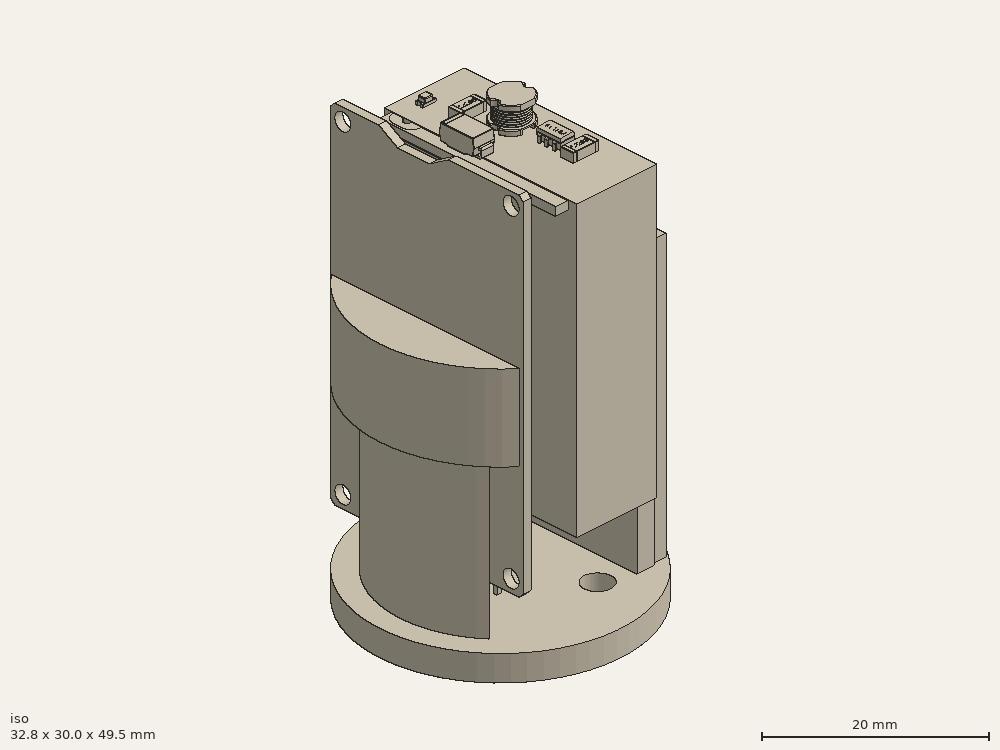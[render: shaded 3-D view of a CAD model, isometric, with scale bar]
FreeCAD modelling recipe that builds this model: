
FCSTD DOCUMENT  (FreeCAD 1.0R39319 (Git))
Label: case
License: All rights reserved
LicenseURL: https://en.wikipedia.org/wiki/All_rights_reserved
objects: Part::Feature×26, Sketcher::SketchObject×12, PartDesign::Pad×8, PartDesign::Pocket×6, PartDesign::Body×2, Assembly::JointGroup×1, Part::Compound2×1, Assembly::AssemblyObject×1
note: 94 computed .brp shape members not serialized (recipe doc carries the construction recipe); baked Part::Feature solids carry a one-line shape summary decoded from their .brp

FEATURE [Assembly::JointGroup] Joints
FEATURE [Part::Feature] Solid  label="SD"
  Placement = pos=(-9.17,6e-15,27) rot=(0.57735,0.57735,0.57735;4.18879rad)
  shape: bbox 4 x 24 x 44.75 mm, 1523 faces (baked)
FEATURE [Part::Feature] Solid024  label="ProMini"
  Placement = pos=(11.482,-0.307405,17.75) rot=(0,1,0;4.71239rad)
  shape: bbox 4.104 x 17.78 x 33.02 mm, 2932 faces (baked)
FEATURE [Part::Feature] Feature  label="mini_dc_dc001"
  Placement = pos=(16,-7.5,27.5) rot=(0,0,1;1.5708rad)
  shape: bbox 11 x 22 x 4.21 mm, 1273 faces, 17 solids (baked)
FEATURE [Sketcher::SketchObject] Sketch001
  ArcFitTolerance = 1e-06
  AttachmentSupport = -> [XY_Plane001]
  FullyConstrained = true
  MakeInternals = false
  MapMode = 5
  sketch-geometry (1):
    g0: Circle CenterX=0 CenterY=0 CenterZ=0 NormalX=0 NormalY=0 NormalZ=1 AngleXU=0 Radius=16.5
  constraints (2):
    c: Diameter(g0) = 33
    c: Coincident(g0,g-1)
FEATURE [PartDesign::Pad] Pad
  Direction = (0,0,1)
  Length = 1
  Length2 = 10
  Profile = -> Sketch001
  ReferenceAxis = -> Sketch001 [N_Axis]
  Refine = true
  Suppressed = false
  Type = 0
FEATURE [Part::Feature] Solid026 .. Solid033  x8 (patterned run collapsed; names and placements below)
  shape: bbox 2.54 x 11.18 x 2.54 mm, 32 faces (baked)
FEATURE [Part::Feature] Solid034
  shape: bbox 5.403 x 0.9032 x 5.403 mm, 256 faces (baked)
FEATURE [Part::Feature] Solid035
  shape: bbox 3.012 x 1.362 x 3.662 mm, 115 faces (baked)
FEATURE [Part::Feature] Solid036
  shape: bbox 2.765 x 1.061 x 0.8748 mm, 38 faces (baked)
FEATURE [Part::Feature] Solid037
  shape: bbox 0.8748 x 1.061 x 2.765 mm, 38 faces (baked)
FEATURE [Part::Feature] Solid038
  shape: bbox 0.8775 x 0.4775 x 2.468 mm, 43 faces (baked)
FEATURE [Part::Feature] Solid039
  shape: bbox 0.8775 x 0.4775 x 2.468 mm, 43 faces (baked)
FEATURE [Part::Feature] Solid040
  shape: bbox 0.8748 x 1.061 x 2.765 mm, 38 faces (baked)
FEATURE [Part::Feature] Solid041
  shape: bbox 0.8748 x 1.061 x 2.765 mm, 38 faces (baked)
FEATURE [Part::Feature] Solid042
  shape: bbox 0.8748 x 1.061 x 2.765 mm, 38 faces (baked)
FEATURE [Part::Feature] Solid043
  shape: bbox 0.8775 x 0.4775 x 2.468 mm, 43 faces (baked)
FEATURE [Part::Feature] Solid044
  shape: bbox 0.8748 x 1.061 x 2.765 mm, 38 faces (baked)
FEATURE [Part::Feature] Solid045
  shape: bbox 0.85 x 0.84 x 1.9 mm, 36 faces (baked)
FEATURE [Part::Feature] Solid046
  shape: bbox 0.8775 x 0.4775 x 2.468 mm, 43 faces (baked)
FEATURE [Part::Feature] Solid047
  shape: bbox 4.2 x 1.693 x 1.6 mm, 44 faces (baked)
FEATURE [Part::Feature] Solid025
  shape: bbox 21.11 x 1.143 x 15.75 mm, 16 faces (baked)
FEATURE [Part::Compound2] Compound  label="mpu"
  Links = -> [Solid025,Solid026,Solid027,Solid028,Solid029,Solid030,Solid031,Solid032,Solid033,Solid034,Solid035,Solid036,Solid037,Solid038,Solid039,Solid040,Solid041,Solid042,Solid043,Solid044,Solid045,Solid046,Solid047]
  Placement = pos=(-17.45,-7.25,-9.5) rot=(0.57735,0.57735,0.57735;2.0944rad)
FEATURE [Sketcher::SketchObject] Sketch002
  ArcFitTolerance = 1e-06
  AttachmentSupport = -> [XY_Plane002]
  FullyConstrained = true
  MakeInternals = false
  MapMode = 5
  sketch-geometry (4):
    g0: LineSegment StartX=0 StartY=0 StartZ=0 EndX=0 EndY=-24 EndZ=0
    g1: LineSegment StartX=0 StartY=-24 StartZ=0 EndX=34 EndY=-24 EndZ=0
    g2: LineSegment StartX=34 StartY=-24 StartZ=0 EndX=34 EndY=0 EndZ=0
    g3: LineSegment StartX=34 StartY=0 StartZ=0 EndX=0 EndY=0 EndZ=0
  constraints (11):
    c: Coincident(g0,g1)
    c: Coincident(g1,g2)
    c: Coincident(g2,g3)
    c: Coincident(g3,g0)
    c: Vertical(g0)
    c: Vertical(g2)
    c: Horizontal(g1)
    c: Horizontal(g3)
    c: Distance(g0,g2) = 34
    c: Distance(g1,g3) = 24
    c: Coincident(g0,g-1)
FEATURE [PartDesign::Pad] Pad001
  Direction = (0,0,1)
  Length = 10
  Length2 = 10
  Profile = -> Sketch002
  ReferenceAxis = -> Sketch002 [N_Axis]
  Refine = true
  Suppressed = false
  Type = 0
FEATURE [PartDesign::Body] Body001  label="lipo"
  AllowCompound = false
  Group = -> [Sketch002,Pad001]
  Origin = -> Origin002
  Placement = pos=(7.5,12,10.07) rot=(0,1,0;4.71239rad)
  Tip = -> Pad001
FEATURE [Sketcher::SketchObject] Sketch003
  ArcFitTolerance = 1e-06
  AttachmentSupport = -> [XY_Plane001]
  FullyConstrained = false
  MakeInternals = false
  MapMode = 5
  sketch-geometry (4):
    g0: LineSegment StartX=-10.1025 StartY=7.19243 StartZ=0 EndX=-10.8313 EndY=7.19243 EndZ=0
    g1: LineSegment StartX=-10.8313 StartY=7.19243 StartZ=0 EndX=-10.8313 EndY=-7.43647 EndZ=0
    g2: LineSegment StartX=-10.8313 StartY=-7.43647 StartZ=0 EndX=-10.1025 EndY=-7.43647 EndZ=0
    g3: LineSegment StartX=-10.1025 StartY=-7.43647 StartZ=0 EndX=-10.1025 EndY=7.19243 EndZ=0
  constraints (8):
    c: Coincident(g0,g1)
    c: Coincident(g1,g2)
    c: Coincident(g2,g3)
    c: Coincident(g3,g0)
    c: Horizontal(g0)
    c: Horizontal(g2)
    c: Vertical(g1)
    c: Vertical(g3)
FEATURE [Sketcher::SketchObject] Sketch004
  ArcFitTolerance = 1e-06
  AttachmentSupport = -> [Pad]
  FullyConstrained = false
  MakeInternals = false
  MapMode = 5
  Placement = pos=(0,0,1) rot=(0,0,1;0rad)
  sketch-geometry (4):
    g0: LineSegment StartX=-10.0742 StartY=4.3685 StartZ=0 EndX=-11.0742 EndY=4.3685 EndZ=0
    g1: LineSegment StartX=-11.0742 StartY=4.3685 StartZ=0 EndX=-11.0742 EndY=-5.47094 EndZ=0
    g2: LineSegment StartX=-11.0742 StartY=-5.47094 StartZ=0 EndX=-10.0742 EndY=-5.47094 EndZ=0
    g3: LineSegment StartX=-10.0742 StartY=-5.47094 StartZ=0 EndX=-10.0742 EndY=4.3685 EndZ=0
  constraints (9):
    c: Coincident(g0,g1)
    c: Coincident(g1,g2)
    c: Coincident(g2,g3)
    c: Coincident(g3,g0)
    c: Horizontal(g0)
    c: Horizontal(g2)
    c: Vertical(g1)
    c: Vertical(g3)
    c: Distance(g1,g3) = 1
FEATURE [PartDesign::Pocket] Pocket
  BaseFeature = -> Pad
  Direction = (0,0,-1)
  Length = 5
  Length2 = 5
  Profile = -> Sketch004
  ReferenceAxis = -> Sketch004 [N_Axis]
  Refine = true
  Suppressed = false
  Type = 0
FEATURE [Sketcher::SketchObject] Sketch005
  ArcFitTolerance = 1e-06
  AttachmentSupport = -> [Pocket]
  FullyConstrained = false
  MakeInternals = false
  MapMode = 5
  Placement = pos=(0,0,1) rot=(0,0,1;0rad)
  sketch-geometry (4):
    g0: LineSegment StartX=9.95573 StartY=8.56673 StartZ=0 EndX=7.83459 EndY=8.56673 EndZ=0
    g1: LineSegment StartX=7.83459 StartY=8.56673 StartZ=0 EndX=7.83459 EndY=-9.23192 EndZ=0
    g2: LineSegment StartX=7.83459 StartY=-9.23192 StartZ=0 EndX=9.95573 EndY=-9.23192 EndZ=0
    g3: LineSegment StartX=9.95573 StartY=-9.23192 StartZ=0 EndX=9.95573 EndY=8.56673 EndZ=0
  constraints (8):
    c: Coincident(g0,g1)
    c: Coincident(g1,g2)
    c: Coincident(g2,g3)
    c: Coincident(g3,g0)
    c: Horizontal(g0)
    c: Horizontal(g2)
    c: Vertical(g1)
    c: Vertical(g3)
FEATURE [PartDesign::Pad] Pad002
  BaseFeature = -> Pocket
  Direction = (0,0,1)
  Length = 30
  Length2 = 10
  Profile = -> Sketch005
  ReferenceAxis = -> Sketch005 [N_Axis]
  Refine = true
  Suppressed = false
  Type = 0
FEATURE [Sketcher::SketchObject] Sketch006
  ArcFitTolerance = 1e-06
  AttachmentSupport = -> [Pad002]
  FullyConstrained = false
  MakeInternals = false
  MapMode = 5
  Placement = pos=(0,0,0) rot=(1,0,0;3.14159rad)
  sketch-geometry (2):
    g0: LineSegment StartX=-9.46997 StartY=8.10814 StartZ=0 EndX=-9.46997 EndY=-8.10814 EndZ=0
    g1: ArcOfCircle CenterX=0 CenterY=0 CenterZ=0 NormalX=0 NormalY=0 NormalZ=1 AngleXU=0 Radius=12.4668 StartAngle=2.43351 EndAngle=3.84967
  constraints (3):
    c: Vertical(g0)
    c: Coincident(g1,g0)
    c: Coincident(g1,g0)
FEATURE [PartDesign::Pad] Pad003
  BaseFeature = -> Pad002
  Direction = (0,0,-1)
  Length = 30
  Length2 = 10
  Profile = -> Sketch006
  ReferenceAxis = -> Sketch006 [N_Axis]
  Refine = true
  Reversed = true
  Suppressed = false
  Type = 0
FEATURE [Sketcher::SketchObject] Sketch007
  ArcFitTolerance = 1e-06
  AttachmentSupport = -> [Pad003]
  FullyConstrained = false
  MakeInternals = false
  MapMode = 5
  Placement = pos=(7.83459,0,0) rot=(0.57735,-0.57735,-0.57735;2.0944rad)
  sketch-geometry (4):
    g0: LineSegment StartX=-10 StartY=6.21939 StartZ=0 EndX=-10 EndY=5.1638 EndZ=0
    g1: LineSegment StartX=-10 StartY=5.1638 StartZ=0 EndX=10 EndY=5.1638 EndZ=0
    g2: LineSegment StartX=10 StartY=5.1638 StartZ=0 EndX=10 EndY=6.21939 EndZ=0
    g3: LineSegment StartX=10 StartY=6.21939 StartZ=0 EndX=-10 EndY=6.21939 EndZ=0
  constraints (8):
    c: Coincident(g0,g1)
    c: Coincident(g1,g2)
    c: Coincident(g2,g3)
    c: Coincident(g3,g0)
    c: Vertical(g0)
    c: Vertical(g2)
    c: Horizontal(g1)
    c: Horizontal(g3)
FEATURE [PartDesign::Pad] Pad004
  BaseFeature = -> Pad003
  Direction = (-1,0,0)
  Length = 3
  Length2 = 10
  Profile = -> Sketch007
  ReferenceAxis = -> Sketch007 [N_Axis]
  Refine = true
  Suppressed = false
  Type = 0
FEATURE [Sketcher::SketchObject] Sketch
  ArcFitTolerance = 1e-06
  AttachmentSupport = -> [Pad004]
  FullyConstrained = false
  MakeInternals = false
  MapMode = 5
  Placement = pos=(0,0,30) rot=(0,0,1;0rad)
  sketch-geometry (2):
    g0: ArcOfCircle CenterX=0 CenterY=-0.00563305 CenterZ=0 NormalX=0 NormalY=0 NormalZ=1 AngleXU=0 Radius=16.4954 StartAngle=2.17527 EndAngle=4.10791
    g1: LineSegment StartX=-9.37485 StartY=13.5667 StartZ=0 EndX=-9.37485 EndY=-13.578 EndZ=0
  constraints (3):
    c: Coincident(g1,g0)
    c: Coincident(g1,g0)
    c: Vertical(g1)
FEATURE [PartDesign::Pad] Pad005
  BaseFeature = -> Pad004
  Direction = (0,0,1)
  Length = 10
  Length2 = 10
  Profile = -> Sketch
  ReferenceAxis = -> Sketch [N_Axis]
  Refine = true
  Reversed = true
  Suppressed = false
  Type = 0
FEATURE [Sketcher::SketchObject] Sketch008
  ArcFitTolerance = 1e-06
  AttachmentSupport = -> [Pad005]
  FullyConstrained = false
  MakeInternals = false
  MapMode = 5
  Placement = pos=(0,0,1) rot=(0,0,1;0rad)
  sketch-geometry (2):
    g0: Circle CenterX=4.36794 CenterY=-7.78214 CenterZ=0 NormalX=0 NormalY=0 NormalZ=1 AngleXU=0 Radius=1.55798
    g1: Circle CenterX=4.35381 CenterY=7.76956 CenterZ=0 NormalX=0 NormalY=0 NormalZ=1 AngleXU=0 Radius=1.55627
FEATURE [PartDesign::Pocket] Pocket001
  BaseFeature = -> Pad005
  Direction = (0,0,-1)
  Length = 5
  Length2 = 5
  Profile = -> Sketch008
  ReferenceAxis = -> Sketch008 [N_Axis]
  Refine = true
  Suppressed = false
  Type = 0
FEATURE [PartDesign::Pad] Pad006
  BaseFeature = -> Pocket001
  Direction = (0,0,-1)
  Length = 2
  Length2 = 10
  Profile = -> Pocket001 [Face2]
  Refine = true
  Suppressed = false
  Type = 0
FEATURE [Sketcher::SketchObject] Sketch009
  ArcFitTolerance = 1e-06
  AttachmentSupport = -> [Pad006]
  FullyConstrained = true
  MakeInternals = false
  MapMode = 5
  Placement = pos=(0,0,-2) rot=(1,0,0;3.14159rad)
  sketch-geometry (2):
    g0: Circle CenterX=0 CenterY=0 CenterZ=0 NormalX=0 NormalY=0 NormalZ=1 AngleXU=0 Radius=15.5
    g1: Circle CenterX=0 CenterY=0 CenterZ=0 NormalX=0 NormalY=0 NormalZ=1 AngleXU=0 Radius=16.5
  constraints (4):
    c: Diameter(g0) = 31
    c: Coincident(g0,g-1)
    c: Diameter(g1) = 33
    c: Coincident(g1,g0)
FEATURE [PartDesign::Pocket] Pocket002
  BaseFeature = -> Pad006
  Direction = (0,0,1)
  Length = 300
  Length2 = 5
  Profile = -> Sketch009
  ReferenceAxis = -> Sketch009 [N_Axis]
  Refine = true
  Suppressed = false
  Type = 0
FEATURE [PartDesign::Pad] Pad007
  BaseFeature = -> Pocket002
  Direction = (0,0,1)
  Length = 4
  Length2 = 10
  Profile = -> Pocket002 [Face21]
  Refine = true
  Suppressed = false
  Type = 0
FEATURE [PartDesign::Pocket] Pocket003
  BaseFeature = -> Pad007
  Direction = (0,0,1)
  Length = 4
  Length2 = 5
  Profile = -> Pad007 [Face15]
  Refine = true
  Suppressed = false
  Type = 0
FEATURE [Sketcher::SketchObject] Sketch010
  ArcFitTolerance = 1e-06
  AttachmentSupport = -> [Pocket003]
  FullyConstrained = true
  MakeInternals = false
  MapMode = 5
  Placement = pos=(0,0,-2) rot=(1,0,0;3.14159rad)
  sketch-geometry (2):
    g0: Circle CenterX=0 CenterY=0 CenterZ=0 NormalX=0 NormalY=0 NormalZ=1 AngleXU=0 Radius=15.5
    g1: Circle CenterX=0 CenterY=0 CenterZ=0 NormalX=0 NormalY=0 NormalZ=1 AngleXU=0 Radius=15
  constraints (4):
    c: Diameter(g0) = 31
    c: Coincident(g0,g-1)
    c: Diameter(g1) = 30
    c: Coincident(g1,g0)
FEATURE [PartDesign::Pocket] Pocket004
  BaseFeature = -> Pocket003
  Direction = (0,0,1)
  Length = 600
  Length2 = 5
  Profile = -> Sketch010
  ReferenceAxis = -> Sketch010 [N_Axis]
  Refine = true
  Suppressed = false
  Type = 0
FEATURE [Sketcher::SketchObject] Sketch011
  ArcFitTolerance = 1e-06
  AttachmentSupport = -> [Pocket004]
  FullyConstrained = false
  MakeInternals = false
  MapMode = 5
  Placement = pos=(0,0,-2) rot=(1,0,0;3.14159rad)
  sketch-geometry (4):
    g0: Circle CenterX=4.33918 CenterY=-7.8017 CenterZ=0 NormalX=0 NormalY=0 NormalZ=1 AngleXU=0 Radius=1.58527
    g1: Circle CenterX=4.33918 CenterY=-7.8017 CenterZ=0 NormalX=0 NormalY=0 NormalZ=1 AngleXU=0 Radius=1.65
    g2: Circle CenterX=4.36352 CenterY=7.76627 CenterZ=0 NormalX=0 NormalY=0 NormalZ=1 AngleXU=0 Radius=1.56339
    g3: Circle CenterX=4.36352 CenterY=7.76627 CenterZ=0 NormalX=0 NormalY=0 NormalZ=1 AngleXU=0 Radius=1.65
  constraints (4):
    c: Diameter(g1) = 3.3
    c: Coincident(g1,g0)
    c: Diameter(g3) = 3.3
    c: Coincident(g3,g2)
FEATURE [PartDesign::Pocket] Pocket005
  BaseFeature = -> Pocket004
  Direction = (0,0,1)
  Length = 8
  Length2 = 5
  Profile = -> Sketch011
  ReferenceAxis = -> Sketch011 [N_Axis]
  Refine = true
  Suppressed = false
  Type = 0
FEATURE [PartDesign::Body] Body  label="Case"
  AllowCompound = false
  Group = -> [Sketch001,Pad,Sketch003,Sketch004,Pocket,Sketch005,Pad002,Sketch006,Pad003,Sketch007,Pad004,Sketch,Pad005,Sketch008,Pocket001,Pad006,Sketch009,Pocket002,Pad007,Pocket003,Sketch010,Pocket004,Sketch011,Pocket005]
  Origin = -> Origin001
  Tip = -> Pocket005
FEATURE [Assembly::AssemblyObject] Assembly
  Group = -> [Joints,Solid,Solid024,Feature,Body,Solid041,Solid034,Solid036,Solid031,Solid042,Solid029,Solid037,Solid035,Solid040,Solid039,Solid025,Solid030,Solid027,Solid033,Solid047,Solid026,Solid032,Solid046,Solid044,Solid045,Solid038,Solid028,Solid043,Compound,Body001]
  Origin = -> Origin
  Type = Assembly
